# Revit family: Metal_Lockers-Salsbury_Industries-65000_66000_Series-3_Wide_Units
name_source: partatom
category: Specialty Equipment
revit_build: Autodesk Revit 2016 (Build: 20150714_1515(x64)
units: mm (PartAtom-declared; Revit-internal decimal feet)

## family parameters
Always vertical = Yes
Cut with Voids When Loaded = No
OmniClass Number = 23.40.00.00
OmniClass Title = Equipment and Furnishings
Part Type = Normal
Room Calculation Point = No
Round Connector Dimension = Use Diameter
Shared = No
Work Plane-Based = No

## types (18) — shared parameters
Assembly Code = C1030310
Door Location D1 = Metal Locker Doors-12 inch with Latch Hasps : Six Tier Door - 6 foot
Hasp Handle Material = Plastic - Salsbury Finish - Black
Hasp Plate Rivet Material = Steel -Salsbury Finish - Polished Steel
Manufacturer = Salsbury Industries
MasterFormat Number = 10 51 13
MasterFormat Title = Lockers
OmniClass 23 Number = 23.40.00.00
Sloping Hood = Metal Locker Sloping Hood : None
Standard Leg Base = Metal Locker Legs - 3 Wide : 6" High - 36" W x 12" D
URL = www.lockers.com
Version = 2.0 (06/30/17)
Width = 36.04 "
Zee Base = Metal Locker Zee Base - 3 Wide : None

## per-type parameters (varying)
| type | Base Height | Compartment Divider Height | Depth | Description | Individual Door Height | Model | OmniClass 23 Title | Sloping Hood Height | Top Compartment Divider | Top Row of Doors | Type Comments | Unit Height |
| 66362 - with Standard 6" High Legs | 6 " | 11.157 " | 12.01 " | 3 Wide - 6 Feet High - 12 Inches Deep | 11.532 " | 66362 | Equipment and Furnishings | 6.625 " | Yes | Yes | Standard Metal Lockers - Six Tier | 72 " |
| 66365 - with Standard 6" High Legs | 6 " | 11.157 " | 15.01 " | 3 Wide - 6 Feet High - 15 Inches Deep | 11.532 " | 66365 | Equipment and Furnishings | 8.682 " | Yes | Yes | Standard Metal Lockers - Six Tier | 72 " |
| 66368 - with Standard 6" High Legs | 6 " | 11.157 " | 18.01 " | 3 Wide - 6 Feet High - 18 Inches Deep | 11.532 " | 66368 | Equipment and Furnishings | 10.739 " | Yes | Yes | Standard Metal Lockers - Six Tier | 72 " |
| 66362 - with 77572 Zee Base and 77550 Lockers without Legs | 4 " | 11.157 " | 12.01 " | 3 Wide - 6 Feet High - 12 Inches Deep with Zee Base and Lockers without Legs | 11.532 " | 66362 with 77572 and 77550 | Equipment and Furnishings | 6.625 " | Yes | Yes | Standard Metal Lockers - Six Tier | 72 " |
| 66365 - with 77575 Zee Base and 77550 Lockers without Legs | 4 " | 11.157 " | 15.01 " | 3 Wide - 6 Feet High - 15 Inches Deep with Zee Base and Lockers without Legs | 11.532 " | 66365 with 77575 and 77550 | Equipment and Furnishings | 8.682 " | Yes | Yes | Standard Metal Lockers - Six Tier | 72 " |
| 66368 - with 77578 Zee Base and 77550 Lockers without Legs | 4 " | 11.157 " | 18.01 " | 3 Wide - 6 Feet High - 18 Inches Deep with Zee Base and Lockers without Legs | 11.532 " | 66368 with 77578 and 77550 | Equipment aqnd Furnishings | 10.739 " | Yes | Yes | Standard Metal Lockers - Six Tier | 72 " |
| 66362 - with 77550 Lockers without Legs | 0 " | 11.157 " | 12.01 " | 3 Wide - 6 Feet High - 12 Inches Deep with Lockers without Legs | 11.532 " | 66362 with 77550 | Equipment and Furnishings | 6.625 " | Yes | Yes | Standard Metal Lockers - Six Tier | 72 " |
| 66365 - with 77550 Lockers without Legs | 0 " | 11.157 " | 15.01 " | 3 Wide - 6 Feet High - 15 Inches Deep with Lockers without Legs | 11.532 " | 66365 with 77550 | Equipment and Furnishings | 8.682 " | Yes | Yes | Standard Metal Lockers - Six Tier | 72 " |
| 66368 - with 77550 Lockers without Legs | 0 " | 11.157 " | 18.01 " | 3 Wide - 6 Feet High - 18 Inches Deep with Lockers without Legs | 11.532 " | 66368 with 77550 | Equipment and Furnishings | 10.739 " | Yes | Yes | Standard Metal Lockers - Six Tier | 72 " |
| 65352 - with Standard 6" High Legs | 6 " | 11.088 " | 12.01 " | 3 Wide - 5 Feet High - 12 Inches Deep | 11.463 " | 65352 | Equipment and Furnishings | 6.625 " | No | No | Standard Metal Lockers - Five Tier | 60 " |
| 65352 - with 77572 Zee Base and 77550 Lockers without Legs | 4 " | 11.088 " | 12.01 " | 3 Wide - 5 Feet High - 12 Inches Deep with Zee Base and Lockers without Legs | 11.463 " | 65352 with 77572 and 77550 | Equipment and Furnishings | 6.625 " | No | No | Standard Metal Lockers - Five Tier | 60 " |
| 65352 - with 77550 Lockers without Legs | 0 " | 11.088 " | 12.01 " | 3 Wide - 5 Feet High - 12 Inches Deep with Lockers without Legs | 11.463 " | 65352 with 77550 | Equipment and Furnishings | 6.625 " | No | No | Standard Metal Lockers - Five Tier | 60 " |
| 65355 - with Standard 6" High Legs | 6 " | 11.088 " | 15.01 " | 3 Wide - 5 Feet High - 15 Inches Deep | 11.463 " | 65355 | Equipment and Furnishings | 8.682 " | No | No | Standard Metal Lockers - Five Tier | 60 " |
| 65355 - with 77575 Zee Base and 77550 Lockers without Legs | 4 " | 11.088 " | 15.01 " | 3 Wide - 5 Feet High - 15 Inches Deep with Zee Base and Lockers without Legs | 11.463 " | 65355 with 77575 and 77550 | Equipment and Furnishings | 8.682 " | No | No | Standard Metal Lockers - Five Tier | 60 " |
| 65355 - with 77550 Lockers without Legs | 0 " | 11.088 " | 15.01 " | 3 Wide - 5 Feet High - 15 Inches Deep with Lockers without Legs | 11.463 " | 65365 with 77550 | Equipment and Furnishings | 8.682 " | No | No | Standard Metal Lockers - Five Tier | 60 " |
| 65358 - with Standard 6" High Legs | 6 " | 11.088 " | 18.01 " | 3 Wide - 5 Feet High - 18 Inches Deep | 11.463 " | 65358 | Equipment and Furnishings | 10.739 " | No | No | Standard Metal Lockers - Five Tier | 60 " |
| 65358 - with 77578 Zee Base and 77550 Lockers without Legs | 4 " | 11.088 " | 18.01 " | 3 Wide - 5 Feet High - 18 Inches Deep with Zee Base and Lockers without Legs | 11.463 " | 65358 with 77578 and 77550 | Equipment and Furnishings | 10.739 " | No | No | Standard Metal Lockers - Five Tier | 60 " |
| 65358 - with 77550 Lockers without Legs | 0 " | 11.088 " | 18.01 " | 3 Wide - 5 Feet High - 18 Inches Deep with Lockers without Legs | 11.463 " | 65358 with 77550 | Equipment and Furnishings | 10.739 " | No | No | Standard Metal Lockers - Five Tier | 60 " |

## geometry (parser evidence)
native form markers: Sweep x49
no freeform markers — native parametric forms only
